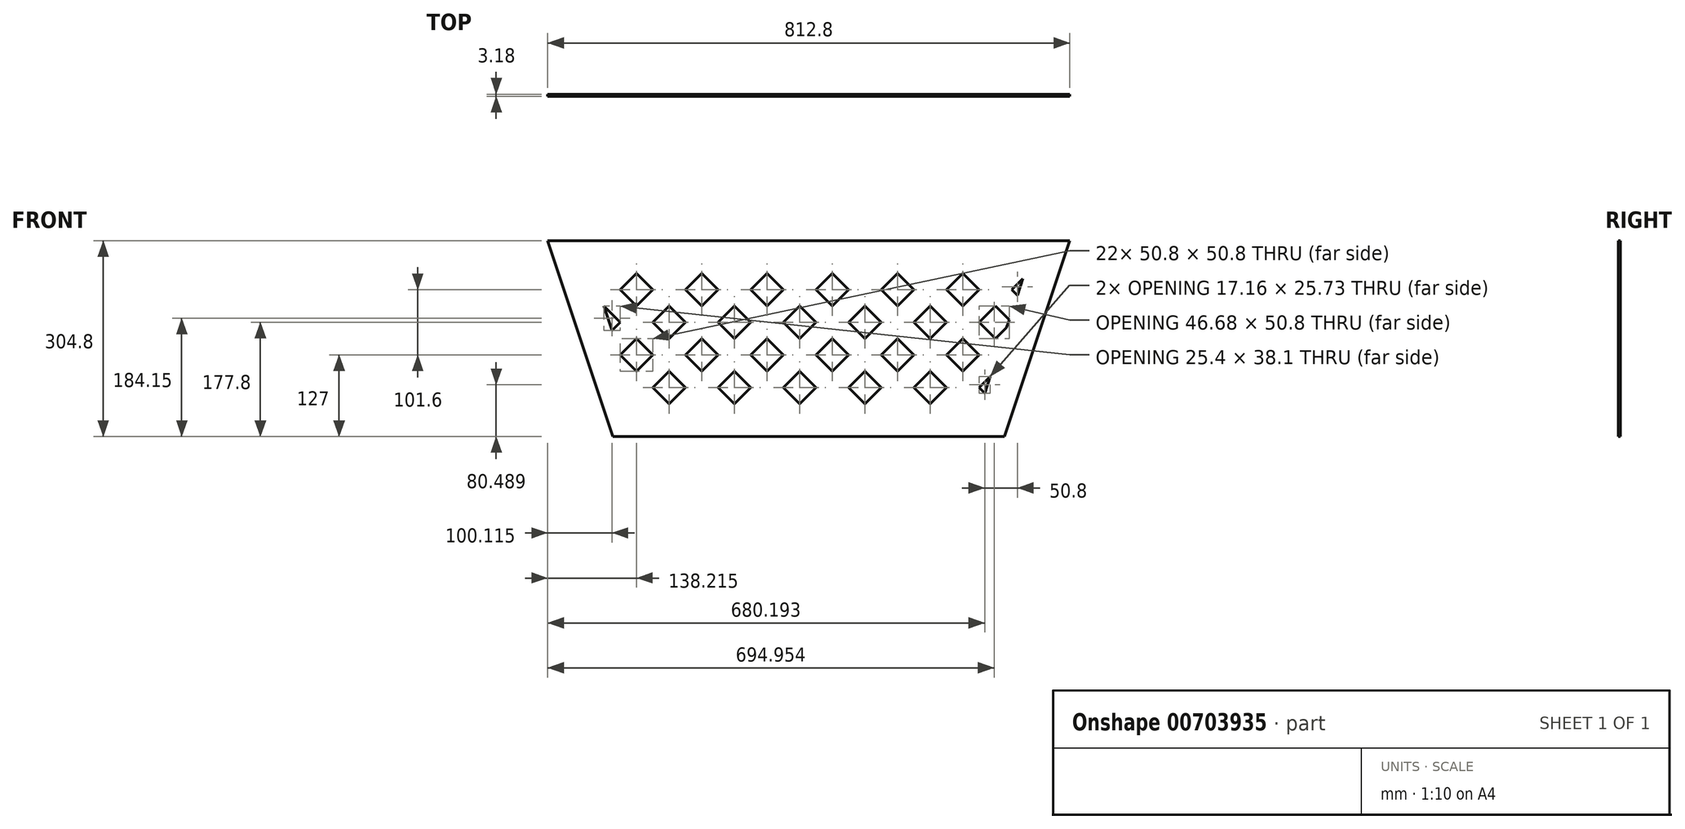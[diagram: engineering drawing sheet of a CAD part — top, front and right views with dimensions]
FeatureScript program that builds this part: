
annotation { "Feature Type Name" : "Feature", "Feature Type Description" : "" }
export const myFeature = defineFeature(function(context is Context, id is Id, definition is map)
    precondition{}
    {
        {
            var Q0;
            Q0=qCreatedBy(makeId("Front.planeOp"),FACE);
            var sketch = newSketch(context, id + "F0", { "sketchPlane" : qUnion([Q0])});
            skLineSegment(sketch, "E0", {"start": v(0, 304.8) * mm, "end": v(-406.4, 304.8) * mm});
            skLineSegment(sketch, "E1", {"start": v(-406.4, 304.8) * mm, "end": v(406.4, 304.8) * mm});
            skLineSegment(sketch, "E2", {"start": v(0, 0) * mm, "end": v(0, -50.8) * mm});
            skLineSegment(sketch, "E3", {"start": v(-256.2, -101.6) * mm, "end": v(-355.6, -101.6) * mm});
            skLineSegment(sketch, "E4", {"start": v(406.4, 304.8) * mm, "end": v(304.8, 0) * mm});
            skLineSegment(sketch, "E5", {"start": v(-304.8, 0) * mm, "end": v(-406.4, 304.8) * mm});
            skLineSegment(sketch, "E6", {"start": v(-335.92, 254) * mm, "end": v(-268.19, 50.8) * mm});
            skLineSegment(sketch, "E7", {"start": v(-268.19, 50.8) * mm, "end": v(268.19, 50.8) * mm});
            skLineSegment(sketch, "E8", {"start": v(335.92, 254) * mm, "end": v(-335.92, 254) * mm});
            skLineSegment(sketch, "E9", {"start": v(335.92, 254) * mm, "end": v(268.19, 50.8) * mm});
            skPoint(sketch, "E10.orphan", {"position": v(0, -101.6) * mm});
            skPoint(sketch, "E11", {"position": v(-215.9, 0) * mm});
            skPoint(sketch, "E12", {"position": v(-88.9, 0) * mm});
            skPoint(sketch, "E13", {"position": v(88.9, 0) * mm});
            skPoint(sketch, "E14", {"position": v(215.9, 0) * mm});
            skLineSegment(sketch, "E15", {"start": v(-217.39, 50.8) * mm, "end": v(-242.79, 76.2) * mm});
            skPoint(sketch, "E16.end.orphan", {"position": v(-391.2, 0) * mm});
            skLineSegment(sketch, "E17.1.0.0", {"start": v(-191.99, 76.2) * mm, "end": v(-217.39, 101.6) * mm});
            skLineSegment(sketch, "E17.2.0.0", {"start": v(-115.79, 50.8) * mm, "end": v(-141.19, 76.2) * mm});
            skLineSegment(sketch, "E17.3.0.0", {"start": v(-90.39, 76.2) * mm, "end": v(-115.79, 101.6) * mm});
            skLineSegment(sketch, "E17.4.0.0", {"start": v(-14.19, 50.8) * mm, "end": v(-39.59, 76.2) * mm});
            skLineSegment(sketch, "E17.5.0.0", {"start": v(11.21, 76.2) * mm, "end": v(-14.19, 101.6) * mm});
            skLineSegment(sketch, "E17.6.0.0", {"start": v(87.41, 50.8) * mm, "end": v(62.01, 76.2) * mm});
            skLineSegment(sketch, "E17.7.0.0", {"start": v(112.81, 76.2) * mm, "end": v(87.41, 101.6) * mm});
            skLineSegment(sketch, "E17.8.0.0", {"start": v(189.01, 50.8) * mm, "end": v(163.61, 76.2) * mm});
            skLineSegment(sketch, "E17.9.0.0", {"start": v(214.41, 76.2) * mm, "end": v(189.01, 101.6) * mm});
            skLineSegment(sketch, "E17.10.0.0", {"start": v(273.8, 67.62) * mm, "end": v(265.21, 76.2) * mm});
            skLineSegment(sketch, "E17.12.0.0", {"start": v(290.61, 152.4) * mm, "end": v(265.21, 177.8) * mm});
            skLineSegment(sketch, "E17.14.0.0", {"start": v(324.6, 220.02) * mm, "end": v(316.01, 228.6) * mm});
            skLineSegment(sketch, "E17.direction1", {"start": v(-420.59, 254) * mm, "end": v(-369.79, 254) * mm, "construction": true});
            skLineSegment(sketch, "E18.3.0.0", {"start": v(-166.59, 254) * mm, "end": v(-191.99, 228.6) * mm});
            skLineSegment(sketch, "E18.4.0.0", {"start": v(-141.19, 228.6) * mm, "end": v(-166.59, 203.2) * mm});
            skLineSegment(sketch, "E18.5.0.0", {"start": v(-64.99, 254) * mm, "end": v(-90.39, 228.6) * mm});
            skLineSegment(sketch, "E18.6.0.0", {"start": v(-39.59, 228.6) * mm, "end": v(-64.99, 203.2) * mm});
            skLineSegment(sketch, "E18.7.0.0", {"start": v(36.61, 254) * mm, "end": v(11.21, 228.6) * mm});
            skLineSegment(sketch, "E18.8.0.0", {"start": v(62.01, 228.6) * mm, "end": v(36.61, 203.2) * mm});
            skLineSegment(sketch, "E18.9.0.0", {"start": v(138.21, 254) * mm, "end": v(112.81, 228.6) * mm});
            skLineSegment(sketch, "E18.10.0.0", {"start": v(163.61, 228.6) * mm, "end": v(138.21, 203.2) * mm});
            skLineSegment(sketch, "E18.11.0.0", {"start": v(239.81, 254) * mm, "end": v(214.41, 228.6) * mm});
            skLineSegment(sketch, "E18.12.0.0", {"start": v(265.21, 228.6) * mm, "end": v(239.81, 203.2) * mm});
            skLineSegment(sketch, "E18.13.0.0", {"start": v(333.17, 245.76) * mm, "end": v(316.01, 228.6) * mm});
            skPoint(sketch, "E19.orphan", {"position": v(-420.59, 50.8) * mm});
            skPoint(sketch, "E20.orphan", {"position": v(-369.79, 50.8) * mm});
            skPoint(sketch, "E21.orphan", {"position": v(-318.99, 50.8) * mm});
            skPoint(sketch, "E22.orphan", {"position": v(290.61, 50.8) * mm});
            skLineSegment(sketch, "E23.trimOffspring", {"start": v(265.21, 127) * mm, "end": v(239.81, 152.4) * mm});
            skPoint(sketch, "E24.orphan", {"position": v(392.21, 50.8) * mm});
            skLineSegment(sketch, "E25.trimOffspring", {"start": v(311.9, 181.92) * mm, "end": v(290.61, 203.2) * mm});
            skPoint(sketch, "E26.orphan", {"position": v(493.81, 50.8) * mm});
            skLineSegment(sketch, "E27.trimOffspring", {"start": v(307.77, 169.56) * mm, "end": v(290.61, 152.4) * mm});
            skPoint(sketch, "E28.orphan", {"position": v(341.41, 254) * mm});
            skPoint(sketch, "E18.direction1.start.orphan", {"position": v(-522.19, 50.8) * mm});
            skLineSegment(sketch, "E29.trimOffspring", {"start": v(-268.19, 203.2) * mm, "end": v(-293.59, 228.6) * mm});
            skLineSegment(sketch, "E30.trimOffspring", {"start": v(-293.59, 177.8) * mm, "end": v(-318.99, 203.2) * mm});
            skLineSegment(sketch, "E31.trimOffspring", {"start": v(-268.19, 152.4) * mm, "end": v(-293.59, 127) * mm});
            skLineSegment(sketch, "E32.trimOffspring", {"start": v(-217.39, 203.2) * mm, "end": v(-242.79, 177.8) * mm});
            skLineSegment(sketch, "E33.trimOffspring", {"start": v(-242.79, 127) * mm, "end": v(-268.19, 101.6) * mm});
            skLineSegment(sketch, "E34.trimOffspring", {"start": v(-268.19, 101.6) * mm, "end": v(-293.59, 127) * mm});
            skLineSegment(sketch, "E35.trimOffspring", {"start": v(-242.79, 127) * mm, "end": v(-268.19, 152.4) * mm});
            skPoint(sketch, "E36.orphan", {"position": v(-166.59, 50.8) * mm});
            skLineSegment(sketch, "E37.trimOffspring", {"start": v(-166.59, 101.6) * mm, "end": v(-191.99, 127) * mm});
            skLineSegment(sketch, "E38.trimOffspring", {"start": v(-217.39, 152.4) * mm, "end": v(-242.79, 177.8) * mm});
            skLineSegment(sketch, "E39.trimOffspring", {"start": v(-191.99, 76.2) * mm, "end": v(-217.39, 50.8) * mm});
            skLineSegment(sketch, "E40.trimOffspring", {"start": v(-217.39, 101.6) * mm, "end": v(-242.79, 76.2) * mm});
            skLineSegment(sketch, "E41.trimOffspring", {"start": v(-141.19, 127) * mm, "end": v(-166.59, 152.4) * mm});
            skLineSegment(sketch, "E42.trimOffspring", {"start": v(-141.19, 127) * mm, "end": v(-166.59, 101.6) * mm});
            skLineSegment(sketch, "E43.trimOffspring", {"start": v(-166.59, 152.4) * mm, "end": v(-191.99, 127) * mm});
            skLineSegment(sketch, "E44.trimOffspring", {"start": v(-191.99, 177.8) * mm, "end": v(-217.39, 203.2) * mm});
            skLineSegment(sketch, "E45.trimOffspring", {"start": v(-191.99, 177.8) * mm, "end": v(-217.39, 152.4) * mm});
            skLineSegment(sketch, "E46.trimOffspring", {"start": v(-242.79, 228.6) * mm, "end": v(-268.19, 254) * mm});
            skPoint(sketch, "E47.orphan", {"position": v(-217.39, 254) * mm});
            skLineSegment(sketch, "E48.trimOffspring", {"start": v(-166.59, 203.2) * mm, "end": v(-191.99, 228.6) * mm});
            skLineSegment(sketch, "E49.trimOffspring", {"start": v(-141.19, 228.6) * mm, "end": v(-166.59, 254) * mm});
            skLineSegment(sketch, "E50.trimOffspring", {"start": v(-115.79, 203.2) * mm, "end": v(-141.19, 177.8) * mm});
            skLineSegment(sketch, "E51.trimOffspring", {"start": v(-90.39, 177.8) * mm, "end": v(-115.79, 152.4) * mm});
            skLineSegment(sketch, "E52.trimOffspring", {"start": v(-90.39, 177.8) * mm, "end": v(-115.79, 203.2) * mm});
            skLineSegment(sketch, "E53.trimOffspring", {"start": v(-115.79, 152.4) * mm, "end": v(-141.19, 177.8) * mm});
            skLineSegment(sketch, "E54.trimOffspring", {"start": v(-115.79, 101.6) * mm, "end": v(-141.19, 76.2) * mm});
            skLineSegment(sketch, "E55.trimOffspring", {"start": v(-90.39, 76.2) * mm, "end": v(-115.79, 50.8) * mm});
            skPoint(sketch, "E56.orphan", {"position": v(-64.99, 50.8) * mm});
            skLineSegment(sketch, "E57.trimOffspring", {"start": v(-64.99, 101.6) * mm, "end": v(-90.39, 127) * mm});
            skLineSegment(sketch, "E58.trimOffspring", {"start": v(-39.59, 127) * mm, "end": v(-64.99, 152.4) * mm});
            skLineSegment(sketch, "E59.trimOffspring", {"start": v(-39.59, 127) * mm, "end": v(-64.99, 101.6) * mm});
            skLineSegment(sketch, "E60.trimOffspring", {"start": v(-64.99, 152.4) * mm, "end": v(-90.39, 127) * mm});
            skPoint(sketch, "E61.orphan", {"position": v(-115.79, 254) * mm});
            skLineSegment(sketch, "E62.trimOffspring", {"start": v(-64.99, 203.2) * mm, "end": v(-90.39, 228.6) * mm});
            skLineSegment(sketch, "E63.trimOffspring", {"start": v(-39.59, 228.6) * mm, "end": v(-64.99, 254) * mm});
            skLineSegment(sketch, "E64.trimOffspring", {"start": v(-14.19, 101.6) * mm, "end": v(-39.59, 76.2) * mm});
            skLineSegment(sketch, "E65.trimOffspring", {"start": v(-14.19, 203.2) * mm, "end": v(-39.59, 177.8) * mm});
            skLineSegment(sketch, "E66.trimOffspring", {"start": v(11.21, 177.8) * mm, "end": v(-14.19, 152.4) * mm});
            skLineSegment(sketch, "E67.trimOffspring", {"start": v(11.21, 177.8) * mm, "end": v(-14.19, 203.2) * mm});
            skLineSegment(sketch, "E68.trimOffspring", {"start": v(-14.19, 152.4) * mm, "end": v(-39.59, 177.8) * mm});
            skLineSegment(sketch, "E69.trimOffspring", {"start": v(11.21, 76.2) * mm, "end": v(-14.19, 50.8) * mm});
            skPoint(sketch, "E70.orphan", {"position": v(36.61, 50.8) * mm});
            skLineSegment(sketch, "E71.trimOffspring", {"start": v(36.61, 101.6) * mm, "end": v(11.21, 127) * mm});
            skPoint(sketch, "E72.orphan", {"position": v(-14.19, 254) * mm});
            skLineSegment(sketch, "E73.trimOffspring", {"start": v(36.61, 203.2) * mm, "end": v(11.21, 228.6) * mm});
            skLineSegment(sketch, "E74.trimOffspring", {"start": v(62.01, 228.6) * mm, "end": v(36.61, 254) * mm});
            skLineSegment(sketch, "E75.trimOffspring", {"start": v(36.61, 152.4) * mm, "end": v(11.21, 127) * mm});
            skPoint(sketch, "E76.orphan", {"position": v(87.41, 254) * mm});
            skLineSegment(sketch, "E77.trimOffspring", {"start": v(62.01, 127) * mm, "end": v(36.61, 101.6) * mm});
            skLineSegment(sketch, "E78.trimOffspring", {"start": v(112.81, 177.8) * mm, "end": v(87.41, 152.4) * mm});
            skLineSegment(sketch, "E79.trimOffspring", {"start": v(87.41, 203.2) * mm, "end": v(62.01, 177.8) * mm});
            skLineSegment(sketch, "E80.trimOffspring", {"start": v(62.01, 127) * mm, "end": v(36.61, 152.4) * mm});
            skLineSegment(sketch, "E81.trimOffspring", {"start": v(87.41, 101.6) * mm, "end": v(62.01, 76.2) * mm});
            skLineSegment(sketch, "E82.trimOffspring", {"start": v(87.41, 152.4) * mm, "end": v(62.01, 177.8) * mm});
            skLineSegment(sketch, "E83.trimOffspring", {"start": v(112.81, 177.8) * mm, "end": v(87.41, 203.2) * mm});
            skPoint(sketch, "E84.orphan", {"position": v(138.21, 50.8) * mm});
            skLineSegment(sketch, "E85.trimOffspring", {"start": v(112.81, 76.2) * mm, "end": v(87.41, 50.8) * mm});
            skLineSegment(sketch, "E86.trimOffspring", {"start": v(138.21, 101.6) * mm, "end": v(112.81, 127) * mm});
            skLineSegment(sketch, "E87.trimOffspring", {"start": v(163.61, 127) * mm, "end": v(138.21, 152.4) * mm});
            skLineSegment(sketch, "E88.trimOffspring", {"start": v(138.21, 152.4) * mm, "end": v(112.81, 127) * mm});
            skLineSegment(sketch, "E89.trimOffspring", {"start": v(163.61, 127) * mm, "end": v(138.21, 101.6) * mm});
            skLineSegment(sketch, "E90.trimOffspring", {"start": v(189.01, 101.6) * mm, "end": v(163.61, 76.2) * mm});
            skLineSegment(sketch, "E91.trimOffspring", {"start": v(138.21, 203.2) * mm, "end": v(112.81, 228.6) * mm});
            skLineSegment(sketch, "E92.trimOffspring", {"start": v(163.61, 228.6) * mm, "end": v(138.21, 254) * mm});
            skLineSegment(sketch, "E93.trimOffspring", {"start": v(189.01, 203.2) * mm, "end": v(163.61, 177.8) * mm});
            skLineSegment(sketch, "E94.trimOffspring", {"start": v(214.41, 177.8) * mm, "end": v(189.01, 152.4) * mm});
            skLineSegment(sketch, "E95.trimOffspring", {"start": v(214.41, 177.8) * mm, "end": v(189.01, 203.2) * mm});
            skLineSegment(sketch, "E96.trimOffspring", {"start": v(189.01, 152.4) * mm, "end": v(163.61, 177.8) * mm});
            skLineSegment(sketch, "E97.trimOffspring", {"start": v(214.41, 76.2) * mm, "end": v(189.01, 50.8) * mm});
            skPoint(sketch, "E98.orphan", {"position": v(239.81, 50.8) * mm});
            skPoint(sketch, "E99.orphan", {"position": v(189.01, 254) * mm});
            skLineSegment(sketch, "E100.trimOffspring", {"start": v(239.81, 203.2) * mm, "end": v(214.41, 228.6) * mm});
            skLineSegment(sketch, "E101.trimOffspring", {"start": v(239.81, 152.4) * mm, "end": v(214.41, 127) * mm});
            skLineSegment(sketch, "E102.trimOffspring", {"start": v(265.21, 127) * mm, "end": v(239.81, 101.6) * mm});
            skLineSegment(sketch, "E103.trimOffspring", {"start": v(265.21, 228.6) * mm, "end": v(239.81, 254) * mm});
            skPoint(sketch, "E104.orphan", {"position": v(290.61, 254) * mm});
            skLineSegment(sketch, "E105.trimOffspring", {"start": v(290.61, 203.2) * mm, "end": v(265.21, 177.8) * mm});
            skLineSegment(sketch, "E106", {"start": v(265.21, 76.2) * mm, "end": v(282.37, 93.36) * mm});
            skLineSegment(sketch, "E107.trimOffspring", {"start": v(239.81, 101.6) * mm, "end": v(214.41, 127) * mm});
            skLineSegment(sketch, "E108", {"start": v(-268.19, 203.2) * mm, "end": v(-242.79, 228.6) * mm});
            skLineSegment(sketch, "E109", {"start": v(-293.59, 228.6) * mm, "end": v(-268.19, 254) * mm});
            skLineSegment(sketch, "E110", {"start": v(-293.59, 177.8) * mm, "end": v(-306.29, 165.1) * mm});
            skPoint(sketch, "E110.endSnap0", {"position": v(-306.29, 190.5) * mm});
            skPoint(sketch, "E111.trimOffspring.end.orphan", {"position": v(355.6, -101.6) * mm});
            skLineSegment(sketch, "E112", {"start": v(-304.8, 0) * mm, "end": v(304.8, 0) * mm});
            skSolve(sketch);
        }
        {
            var Q0;
            {var subQ20=sQuery(id+"F0.wireOp",EDGE,"E4");Q0=makeQuery(id+"F0.imprint","IMPRINT",FACE,{"disambiguationData":[TD([[makeQuery(id+"F0.imprint","IMPRINT",EDGE,{"derivedFrom":subQ20}),-1.0]])]});}
            var Q1;
            {var subQ11=sQuery(id+"F0.wireOp",EDGE,"E15");Q1=makeQuery(id+"F0.imprint","IMPRINT",FACE,{"disambiguationData":[TD([[makeQuery(id+"F0.imprint","IMPRINT",EDGE,{"derivedFrom":subQ11}),1.0]])]});}
            extrude(context, id + "F1", {"entities" : qUnion([Q0, Q1]), "depth" : 3.17 * mm, "offsetDistance" : 25.4 * mm});
        }
    });
